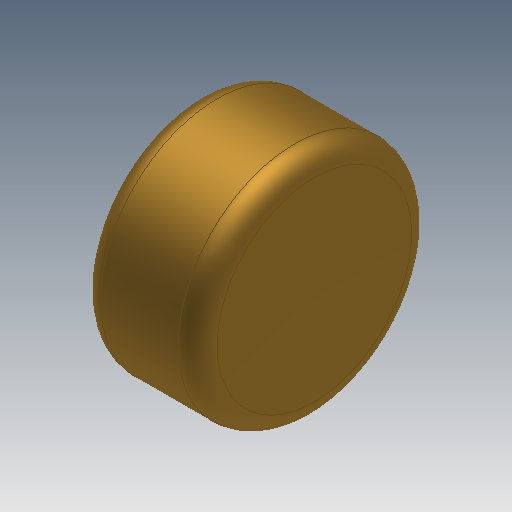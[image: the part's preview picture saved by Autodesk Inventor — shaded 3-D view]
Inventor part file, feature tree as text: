
AUTODESK INVENTOR PART (.ipt)
format: ipt  version: 2018 (Build 220112000, 112)  size: 136,704 bytes
history: native  units: mm
features: extrude x1, fillet x1, sketch x1
ambient origin geometry x8: Origin, YZ Plane, XZ Plane, XY Plane, X Axis, Y Axis, Z Axis, Center Point
bodies: Solid1 (feature_tree)
feature tree (3):
  extrude  "Extrusion1"  Depth=3.0mm
  fillet  "Fillet1"  [1 undecoded]
  sketch  "Sketch1"  dims[d0=6.0mm d1=3.0mm d2=0.0mm d3=0.5mm]
note: 1 required parameter value undecoded (feature->parameter linkage not recoverable at this tier; creation-order binding heuristic only, values carry confidence <= 0.55)
